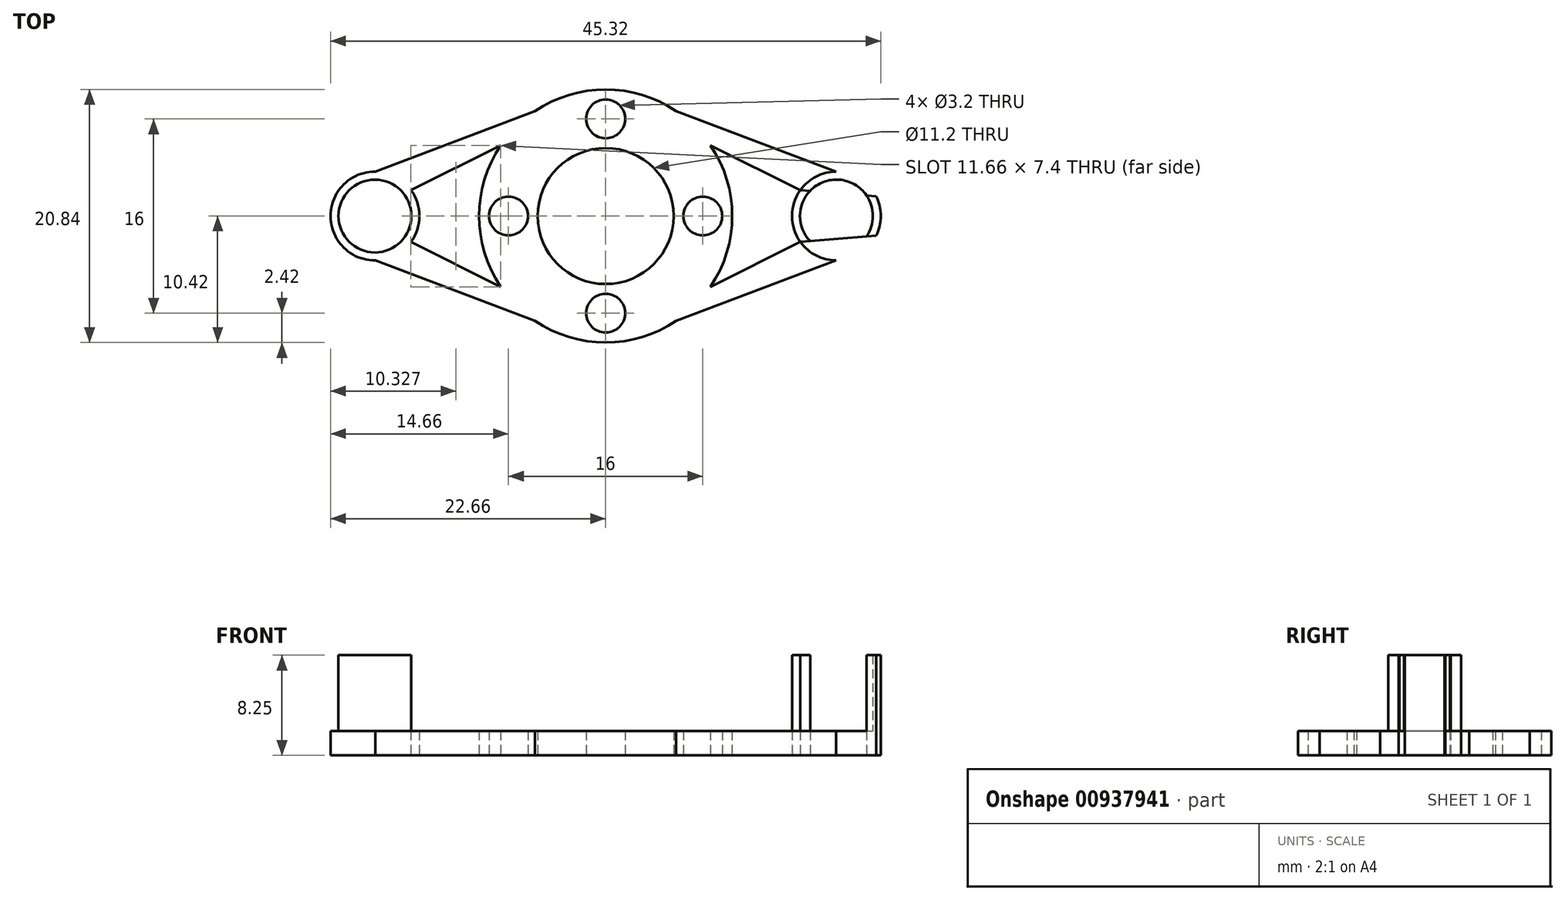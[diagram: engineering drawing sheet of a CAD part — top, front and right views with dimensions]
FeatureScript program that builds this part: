
annotation { "Feature Type Name" : "Feature", "Feature Type Description" : "" }
export const myFeature = defineFeature(function(context is Context, id is Id, definition is map)
    precondition{}
    {
        {
            var Q0;
            Q0=qCreatedBy(makeId("Top.planeOp"),FACE);
            var sketch = newSketch(context, id + "F0", { "sketchPlane" : qUnion([Q0])});
            skPoint(sketch, "E0.middle", {"position": v(0, 0) * mm});
            skCircle(sketch, "E1", {"center": v(-19, 0) * mm, "radius": 3 * mm});
            skCircle(sketch, "E2.MirrorC", {"center": v(19, 0) * mm, "radius": 3 * mm});
            skCircle(sketch, "E3", {"center": v(0, 0) * mm, "radius": 5.6 * mm});
            skCircle(sketch, "E4", {"center": v(8, 0) * mm, "radius": 1.6 * mm});
            skCircle(sketch, "E5.MirrorC", {"center": v(-8, 0) * mm, "radius": 1.6 * mm});
            skCircle(sketch, "E6", {"center": v(-19, 0) * mm, "radius": 3.66 * mm});
            skCircle(sketch, "E7.MirrorC", {"center": v(19, 0) * mm, "radius": 3.66 * mm});
            skCircle(sketch, "E8", {"center": v(0, 0) * mm, "radius": 10.42 * mm});
            skCircle(sketch, "E9", {"center": v(0, -8) * mm, "radius": 1.6 * mm});
            skCircle(sketch, "E10.MirrorC", {"center": v(0, 8) * mm, "radius": 1.6 * mm});
            skLineSegment(sketch, "E11", {"start": v(-22.27, 1.63) * mm, "end": v(-10.08, 2.62) * mm});
            skLineSegment(sketch, "E12.MirrorCS", {"start": v(-22.27, -1.63) * mm, "end": v(-10.08, -2.62) * mm});
            skLineSegment(sketch, "E13.MirrorCS", {"start": v(22.27, 1.63) * mm, "end": v(10.08, 2.62) * mm});
            skLineSegment(sketch, "E14.MirrorCS", {"start": v(22.27, -1.63) * mm, "end": v(10.08, -2.62) * mm});
            skLineSegment(sketch, "E15", {"start": v(-18.97, 3.66) * mm, "end": v(-5.81, 8.64) * mm});
            skLineSegment(sketch, "E16", {"start": v(-16.03, 2.14) * mm, "end": v(-8.63, 5.83) * mm});
            skLineSegment(sketch, "E17.MirrorCS", {"start": v(-16.03, -2.14) * mm, "end": v(-8.63, -5.83) * mm});
            skLineSegment(sketch, "E18.MirrorCS", {"start": v(-18.97, -3.66) * mm, "end": v(-5.81, -8.64) * mm});
            skLineSegment(sketch, "E19.MirrorCS", {"start": v(16.03, 2.14) * mm, "end": v(8.63, 5.83) * mm});
            skLineSegment(sketch, "E20.MirrorCS", {"start": v(18.97, 3.66) * mm, "end": v(5.81, 8.64) * mm});
            skLineSegment(sketch, "E21.MirrorCS", {"start": v(18.97, -3.66) * mm, "end": v(5.81, -8.64) * mm});
            skLineSegment(sketch, "E22.MirrorCS", {"start": v(16.03, -2.14) * mm, "end": v(8.63, -5.83) * mm});
            skSolve(sketch);
        }
        {
            var Q0;
            {var subQ0=sQuery(id+"F0.wireOp",EDGE,"E15");Q0=makeQuery(id+"F0.imprint","IMPRINT",FACE,{"disambiguationData":[TD([[makeQuery(id+"F0.imprint","IMPRINT",EDGE,{"derivedFrom":subQ0}),-1.0]])]});}
            var Q1;
            Q1=makeQuery(id+"F0.imprint","IMPRINT",FACE,{"disambiguationData":[TD([[makeQuery(id+"F0.imprint","IMPRINT",EDGE,{"derivedFrom":sQuery(id+"F0.wireOp",EDGE,"E3")}),-1.0]])]});
            var Q2;
            {var subQ0=sQuery(id+"F0.wireOp",EDGE,"E17.MirrorCS");Q2=makeQuery(id+"F0.imprint","IMPRINT",FACE,{"disambiguationData":[TD([[makeQuery(id+"F0.imprint","IMPRINT",EDGE,{"derivedFrom":subQ0}),-1.0]])]});}
            var Q3;
            {var subQ0=sQuery(id+"F0.wireOp",EDGE,"E12.MirrorCS");var subQ3=sQuery(id+"F0.wireOp",EDGE,"E1");var subQ4=makeQuery(id+"F0.imprint","INTERSECT",VERTEX,{"disambiguationData":[OD(0.0)],"derivedFrom":[subQ3,subQ0]});Q3=makeQuery(id+"F0.imprint","IMPRINT",FACE,{"disambiguationData":[TD([[makeQuery(id+"F0.imprint","IMPRINT",EDGE,{"disambiguationData":[TD([[subQ4,-1.0]])],"derivedFrom":subQ3}),-1.0]])]});}
            var Q4;
            {var subQ0=sQuery(id+"F0.wireOp",EDGE,"E11");var subQ1=sQuery(id+"F0.wireOp",EDGE,"E1");var subQ2=makeQuery(id+"F0.imprint","INTERSECT",VERTEX,{"disambiguationData":[OD(0.0)],"derivedFrom":[subQ1,subQ0]});Q4=makeQuery(id+"F0.imprint","IMPRINT",FACE,{"disambiguationData":[TD([[makeQuery(id+"F0.imprint","IMPRINT",EDGE,{"disambiguationData":[TD([[subQ2,-1.0]])],"derivedFrom":subQ1}),-1.0]])]});}
            var Q5;
            {var subQ0=sQuery(id+"F0.wireOp",EDGE,"E11");var subQ3=sQuery(id+"F0.wireOp",EDGE,"E1");var subQ4=makeQuery(id+"F0.imprint","INTERSECT",VERTEX,{"disambiguationData":[OD(0.0)],"derivedFrom":[subQ3,subQ0]});Q5=makeQuery(id+"F0.imprint","IMPRINT",FACE,{"disambiguationData":[TD([[makeQuery(id+"F0.imprint","IMPRINT",EDGE,{"disambiguationData":[TD([[subQ4,1.0]])],"derivedFrom":subQ3}),-1.0]])]});}
            var Q6;
            {var subQ0=sQuery(id+"F0.wireOp",EDGE,"E11");var subQ1=sQuery(id+"F0.wireOp",EDGE,"E1");var subQ2=makeQuery(id+"F0.imprint","INTERSECT",VERTEX,{"disambiguationData":[OD(1.0)],"derivedFrom":[subQ1,subQ0]});Q6=makeQuery(id+"F0.imprint","IMPRINT",FACE,{"disambiguationData":[TD([[makeQuery(id+"F0.imprint","IMPRINT",EDGE,{"disambiguationData":[TD([[subQ2,1.0]])],"derivedFrom":subQ1}),-1.0]])]});}
            var Q7;
            {var subQ0=sQuery(id+"F0.wireOp",EDGE,"E21.MirrorCS");Q7=makeQuery(id+"F0.imprint","IMPRINT",FACE,{"disambiguationData":[TD([[makeQuery(id+"F0.imprint","IMPRINT",EDGE,{"derivedFrom":subQ0}),-1.0]])]});}
            var Q8;
            {var subQ0=sQuery(id+"F0.wireOp",EDGE,"E19.MirrorCS");Q8=makeQuery(id+"F0.imprint","IMPRINT",FACE,{"disambiguationData":[TD([[makeQuery(id+"F0.imprint","IMPRINT",EDGE,{"derivedFrom":subQ0}),-1.0]])]});}
            var Q9;
            {var subQ0=sQuery(id+"F0.wireOp",EDGE,"E13.MirrorCS");var subQ3=sQuery(id+"F0.wireOp",EDGE,"E2.MirrorC");var subQ4=makeQuery(id+"F0.imprint","INTERSECT",VERTEX,{"disambiguationData":[OD(0.0)],"derivedFrom":[subQ3,subQ0]});Q9=makeQuery(id+"F0.imprint","IMPRINT",FACE,{"disambiguationData":[TD([[makeQuery(id+"F0.imprint","IMPRINT",EDGE,{"disambiguationData":[TD([[subQ4,1.0]])],"derivedFrom":subQ3}),1.0]])]});}
            var Q10;
            {var subQ0=sQuery(id+"F0.wireOp",EDGE,"E13.MirrorCS");var subQ1=sQuery(id+"F0.wireOp",EDGE,"E2.MirrorC");var subQ2=makeQuery(id+"F0.imprint","INTERSECT",VERTEX,{"disambiguationData":[OD(1.0)],"derivedFrom":[subQ1,subQ0]});Q10=makeQuery(id+"F0.imprint","IMPRINT",FACE,{"disambiguationData":[TD([[makeQuery(id+"F0.imprint","IMPRINT",EDGE,{"disambiguationData":[TD([[subQ2,1.0]])],"derivedFrom":subQ1}),1.0]])]});}
            var Q11;
            {var subQ0=sQuery(id+"F0.wireOp",EDGE,"E14.MirrorCS");var subQ3=sQuery(id+"F0.wireOp",EDGE,"E2.MirrorC");var subQ4=makeQuery(id+"F0.imprint","INTERSECT",VERTEX,{"disambiguationData":[OD(0.0)],"derivedFrom":[subQ3,subQ0]});Q11=makeQuery(id+"F0.imprint","IMPRINT",FACE,{"disambiguationData":[TD([[makeQuery(id+"F0.imprint","IMPRINT",EDGE,{"disambiguationData":[TD([[subQ4,-1.0]])],"derivedFrom":subQ3}),1.0]])]});}
            var Q12;
            {var subQ0=sQuery(id+"F0.wireOp",EDGE,"E13.MirrorCS");var subQ1=sQuery(id+"F0.wireOp",EDGE,"E2.MirrorC");var subQ2=makeQuery(id+"F0.imprint","INTERSECT",VERTEX,{"disambiguationData":[OD(0.0)],"derivedFrom":[subQ1,subQ0]});Q12=makeQuery(id+"F0.imprint","IMPRINT",FACE,{"disambiguationData":[TD([[makeQuery(id+"F0.imprint","IMPRINT",EDGE,{"disambiguationData":[TD([[subQ2,-1.0]])],"derivedFrom":subQ1}),1.0]])]});}
            extrude(context, id + "F1", {"entities" : qUnion([Q0, Q1, Q2, Q3, Q4, Q5, Q6, Q7, Q8, Q9, Q10, Q11, Q12]), "depth" : 2 * mm, "offsetDistance" : 25 * mm});
        }
        {
            var Q0;
            Q0=makeQuery(id+"F0.imprint","IMPRINT",FACE,{"disambiguationData":[TD([[makeQuery(id+"F0.imprint","IMPRINT",EDGE,{"derivedFrom":sQuery(id+"F0.wireOp",EDGE,"E1")}),1.0]])]});
            var Q1;
            Q1=makeQuery(id+"F0.imprint","IMPRINT",FACE,{"disambiguationData":[TD([[makeQuery(id+"F0.imprint","IMPRINT",EDGE,{"derivedFrom":sQuery(id+"F0.wireOp",EDGE,"E2.MirrorC")}),-1.0]])]});
            var Q2;
            {var subQ0=sQuery(id+"F0.wireOp",EDGE,"E11");var subQ1=sQuery(id+"F0.wireOp",EDGE,"E1");var subQ2=makeQuery(id+"F0.imprint","INTERSECT",VERTEX,{"disambiguationData":[OD(0.0)],"derivedFrom":[subQ1,subQ0]});Q2=makeQuery(id+"F0.imprint","IMPRINT",FACE,{"disambiguationData":[TD([[makeQuery(id+"F0.imprint","IMPRINT",EDGE,{"disambiguationData":[TD([[subQ2,1.0]])],"derivedFrom":subQ1}),1.0]])]});}
            var Q3;
            {var subQ0=sQuery(id+"F0.wireOp",EDGE,"E12.MirrorCS");var subQ1=sQuery(id+"F0.wireOp",EDGE,"E1");var subQ2=makeQuery(id+"F0.imprint","INTERSECT",VERTEX,{"disambiguationData":[OD(0.0)],"derivedFrom":[subQ1,subQ0]});Q3=makeQuery(id+"F0.imprint","IMPRINT",FACE,{"disambiguationData":[TD([[makeQuery(id+"F0.imprint","IMPRINT",EDGE,{"disambiguationData":[TD([[subQ2,-1.0]])],"derivedFrom":subQ1}),1.0]])]});}
            var Q4;
            {var subQ0=sQuery(id+"F0.wireOp",EDGE,"E14.MirrorCS");var subQ1=sQuery(id+"F0.wireOp",EDGE,"E2.MirrorC");var subQ2=makeQuery(id+"F0.imprint","INTERSECT",VERTEX,{"disambiguationData":[OD(0.0)],"derivedFrom":[subQ1,subQ0]});Q4=makeQuery(id+"F0.imprint","IMPRINT",FACE,{"disambiguationData":[TD([[makeQuery(id+"F0.imprint","IMPRINT",EDGE,{"disambiguationData":[TD([[subQ2,-1.0]])],"derivedFrom":subQ1}),-1.0]])]});}
            var Q5;
            {var subQ0=sQuery(id+"F0.wireOp",EDGE,"E13.MirrorCS");var subQ1=sQuery(id+"F0.wireOp",EDGE,"E2.MirrorC");var subQ2=makeQuery(id+"F0.imprint","INTERSECT",VERTEX,{"disambiguationData":[OD(0.0)],"derivedFrom":[subQ1,subQ0]});Q5=makeQuery(id+"F0.imprint","IMPRINT",FACE,{"disambiguationData":[TD([[makeQuery(id+"F0.imprint","IMPRINT",EDGE,{"disambiguationData":[TD([[subQ2,1.0]])],"derivedFrom":subQ1}),-1.0]])]});}
            extrude(context, id + "F2", {"entities" : qUnion([Q0, Q1, Q2, Q3, Q4, Q5]), "operationType" : NewBodyOperationType.ADD, "depth" : 8.25 * mm, "offsetDistance" : 25 * mm});
        }
    });
